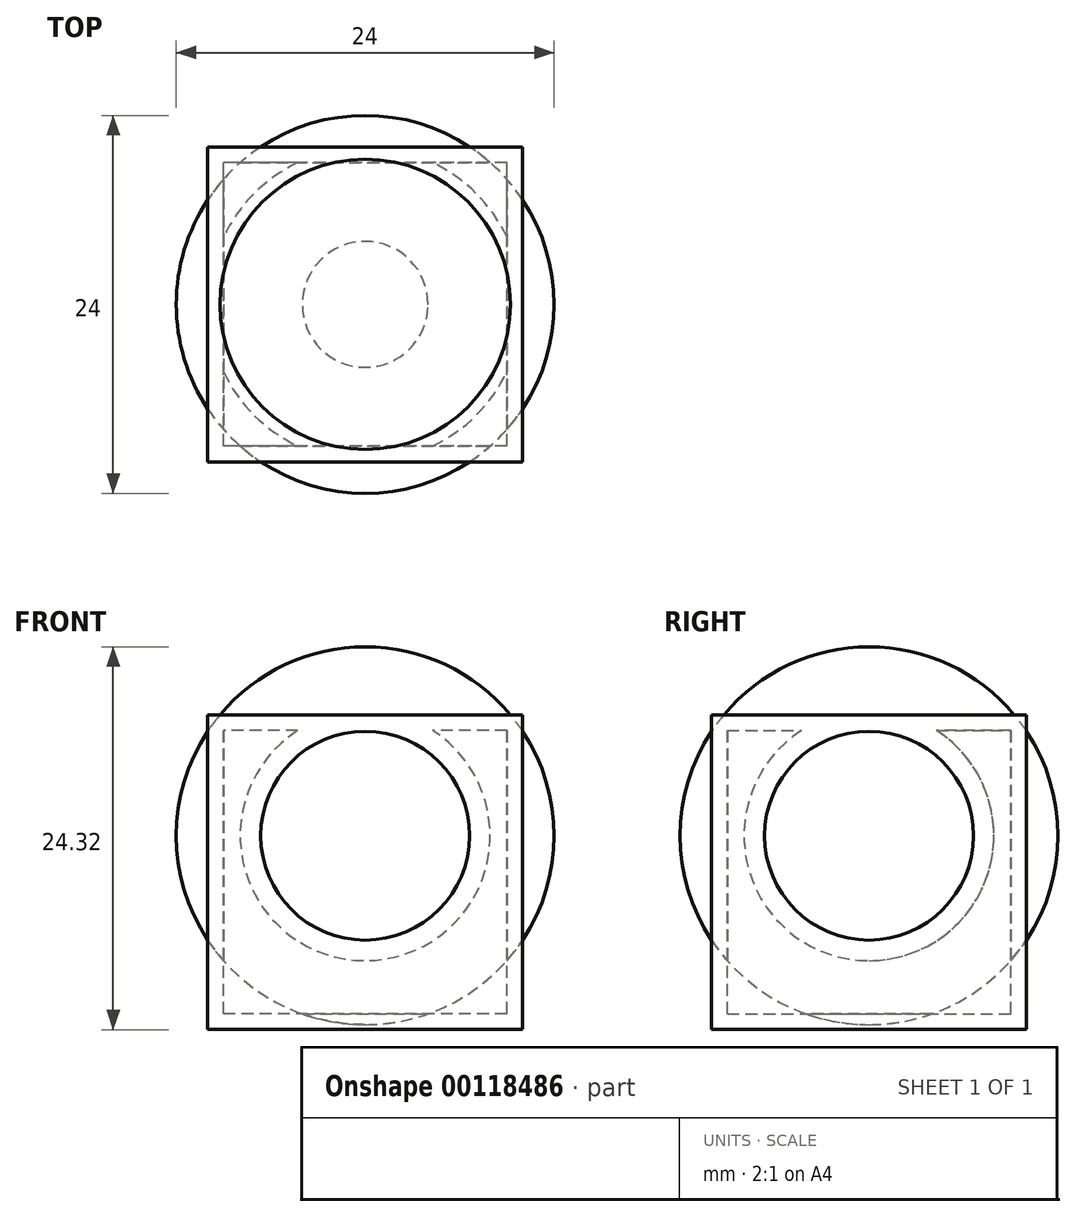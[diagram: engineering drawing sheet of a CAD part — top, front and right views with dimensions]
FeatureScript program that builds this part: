
annotation { "Feature Type Name" : "Feature", "Feature Type Description" : "" }
export const myFeature = defineFeature(function(context is Context, id is Id, definition is map)
    precondition{}
    {
        {
            var Q0;
            Q0=qCreatedBy(makeId("Front.planeOp"),FACE);
            var sketch = newSketch(context, id + "F0", { "sketchPlane" : qUnion([Q0])});
            skLineSegment(sketch, "E0", {"start": v(0, 12) * mm, "end": v(0, -12) * mm});
            skArc(sketch, "E1", {"start": v(0, -12) * mm, "mid": v(12, 0) * mm, "end": v(0, 12) * mm});
            skSolve(sketch);
        }
        {
            var Q0;
            Q0 = qSketchRegion(id + "F0", true);
            var Q1;
            Q1=sQuery(id+"F0.wireOp",EDGE,"E0");
            revolve(context, id + "F1", {"entities" : qUnion([Q0]), "axis" : qUnion([Q1]), "revolveType" : RevolveType.FULL});
        }
        {
            var Q0;
            Q0=qCreatedBy(makeId("Front.planeOp"),FACE);
            var sketch = newSketch(context, id + "F2", { "sketchPlane" : qUnion([Q0])});
            skLineSegment(sketch, "E2.bottom", {"start": v(10, -12.32) * mm, "end": v(-10, -12.32) * mm});
            skLineSegment(sketch, "E2.top", {"start": v(10, 7.68) * mm, "end": v(-10, 7.68) * mm});
            skLineSegment(sketch, "E2.left", {"start": v(10, -12.32) * mm, "end": v(10, 7.68) * mm});
            skLineSegment(sketch, "E2.right", {"start": v(-10, -12.32) * mm, "end": v(-10, 7.68) * mm});
            skPoint(sketch, "E2.middle", {"position": v(0, -2.32) * mm});
            skSolve(sketch);
        }
        {
            var Q0;
            Q0 = qSketchRegion(id + "F2", true);
            extrude(context, id + "F3", {"entities" : qUnion([Q0]), "endBound" : BoundingType.SYMMETRIC, "depth" : 20 * mm});
        }
        {
            var Q0;
            Q0=makeQuery(id+"F3.opExtrude","SWEPT_FACE",FACE,{"disambiguationData":[OSD([sQuery(id+"F2.wireOp",EDGE,"E2.bottom")])]});
            var Q1;
            Q1=makeQuery(id+"F3.opExtrude","SWEPT_BODY",BODY,{"disambiguationData":[OSD([sQuery(id+"F2.wireOp",EDGE,"E2.bottom"),sQuery(id+"F2.wireOp",EDGE,"E2.top"),sQuery(id+"F2.wireOp",EDGE,"E2.left"),sQuery(id+"F2.wireOp",EDGE,"E2.right")])]});
            shell(context, id + "F4", {"isHollow" : true, "entities" : qUnion([Q0]), "parts" : qUnion([Q1]), "thickness" : 1 * mm});
        }
        {
            var Q0;
            Q0=makeQuery(id+"F1.opRevolve","SWEPT_BODY",BODY,{"disambiguationData":[OSD([sQuery(id+"F0.wireOp",EDGE,"E0"),sQuery(id+"F0.wireOp",EDGE,"E1")])]});
            var Q1;
            Q1=makeQuery(id+"F3.opExtrude","SWEPT_BODY",BODY,{"disambiguationData":[OSD([sQuery(id+"F2.wireOp",EDGE,"E2.bottom"),sQuery(id+"F2.wireOp",EDGE,"E2.top"),sQuery(id+"F2.wireOp",EDGE,"E2.left"),sQuery(id+"F2.wireOp",EDGE,"E2.right")])]});
            booleanBodies(context, id + "F5", {"operationType" : BooleanOperationType.SUBTRACTION, "tools" : qUnion([Q0]), "targets" : qUnion([Q1]), "keepTools" : true});
        }
    });
